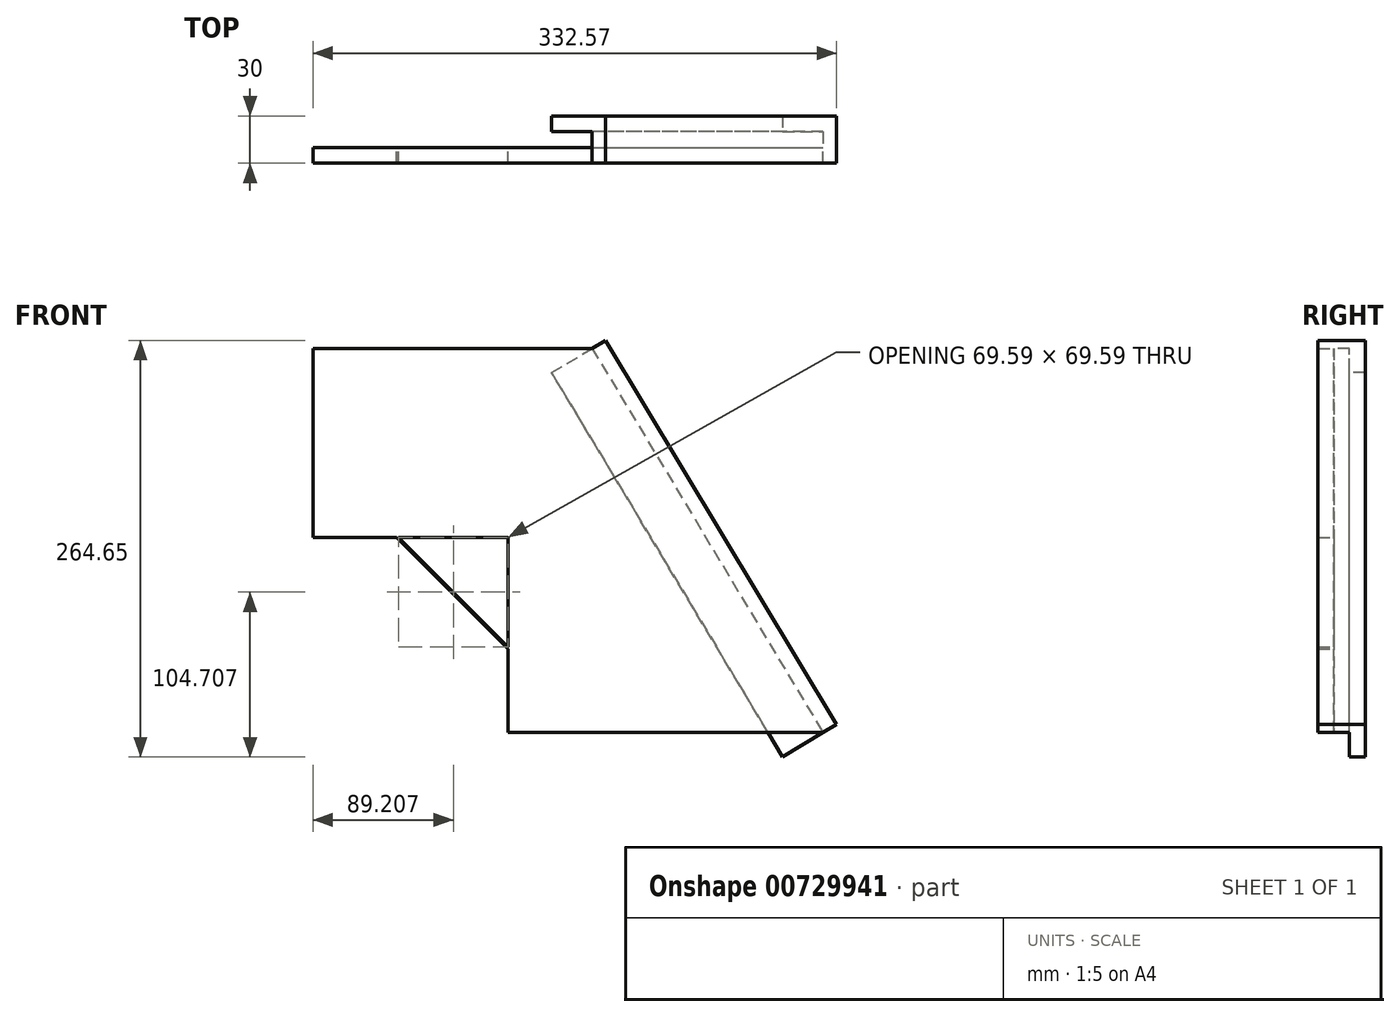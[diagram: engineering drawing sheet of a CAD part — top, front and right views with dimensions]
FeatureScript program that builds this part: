
annotation { "Feature Type Name" : "Feature", "Feature Type Description" : "" }
export const myFeature = defineFeature(function(context is Context, id is Id, definition is map)
    precondition{}
    {
        {
            var Q0;
            Q0=qCreatedBy(makeId("Front.planeOp"),FACE);
            var sketch = newSketch(context, id + "F0", { "sketchPlane" : qUnion([Q0])});
            skLineSegment(sketch, "E0", {"start": v(-68, 0) * mm, "end": v(-68, 120) * mm});
            skLineSegment(sketch, "E1", {"start": v(-68, 120) * mm, "end": v(109.36, 120) * mm});
            skLineSegment(sketch, "E2", {"start": v(109.36, 120) * mm, "end": v(256, -124.05) * mm});
            skLineSegment(sketch, "E3", {"start": v(56, -124.05) * mm, "end": v(56, 0) * mm});
            skLineSegment(sketch, "E4", {"start": v(56, 0) * mm, "end": v(-68, 0) * mm});
            skLineSegment(sketch, "E5", {"start": v(74.71, -80) * mm, "end": v(-76.05, -80) * mm, "construction": true});
            skLineSegment(sketch, "E6", {"start": v(-40, 25) * mm, "end": v(85.18, -100.18) * mm});
            skLineSegment(sketch, "E7", {"start": v(56, -124.05) * mm, "end": v(256, -124.05) * mm});
            skLineSegment(sketch, "E8", {"start": v(-40, 25) * mm, "end": v(-39.3, 25.7) * mm});
            skLineSegment(sketch, "E9", {"start": v(-39.3, 25.7) * mm, "end": v(85.89, -99.47) * mm});
            skLineSegment(sketch, "E10", {"start": v(85.89, -99.47) * mm, "end": v(85.18, -100.18) * mm});
            skSolve(sketch);
        }
        {
            var Q0;
            Q0 = qSketchRegion(id + "F0", true);
            var Q1;
            Q1=makeQuery(id+"F0.imprint","IMPRINT",FACE,{"disambiguationData":[TD([[makeQuery(id+"F0.imprint","IMPRINT",EDGE,{"derivedFrom":sQuery(id+"F0.wireOp",EDGE,"E0")}),-1.0]])]});
            extrude(context, id + "F1", {"entities" : qUnion([Q0, Q1]), "depth" : 10 * mm, "offsetDistance" : 25 * mm});
        }
        {
            var Q0;
            Q0=makeQuery(id+"F1.opExtrude","CAP_FACE",FACE,{"disambiguationData":[OSD([sQuery(id+"F0.wireOp",EDGE,"E0"),sQuery(id+"F0.wireOp",EDGE,"E1"),sQuery(id+"F0.wireOp",EDGE,"E2"),sQuery(id+"F0.wireOp",EDGE,"E3"),sQuery(id+"F0.wireOp",EDGE,"E4"),sQuery(id+"F0.wireOp",EDGE,"E6"),sQuery(id+"F0.wireOp",EDGE,"E7"),sQuery(id+"F0.wireOp",EDGE,"E9")])],"isStart":false});
            var sketch = newSketch(context, id + "F2", { "sketchPlane" : qUnion([Q0])});
            skLineSegment(sketch, "E11", {"start": v(109.36, 120) * mm, "end": v(117.93, 125.15) * mm});
            skLineSegment(sketch, "E12", {"start": v(117.93, 125.15) * mm, "end": v(264.57, -118.9) * mm});
            skLineSegment(sketch, "E13", {"start": v(264.57, -118.9) * mm, "end": v(256, -124.05) * mm});
            skLineSegment(sketch, "E14", {"start": v(256, -124.05) * mm, "end": v(109.36, 120) * mm});
            skSolve(sketch);
        }
        {
            var Q0;
            Q0=makeQuery(id+"F2.imprint","IMPRINT",FACE,{"disambiguationData":[TD([[makeQuery(id+"F2.imprint","IMPRINT",EDGE,{"derivedFrom":sQuery(id+"F2.wireOp",EDGE,"E11")}),-1.0]])]});
            extrude(context, id + "F3", {"entities" : qUnion([Q0]), "operationType" : NewBodyOperationType.ADD, "oppositeDirection" : true, "depth" : 30 * mm, "offsetDistance" : 25 * mm});
        }
        {
            var Q0;
            Q0=makeQuery(id+"F3.opExtrude","SWEPT_FACE",FACE,{"disambiguationData":[OSD([sQuery(id+"F2.wireOp",EDGE,"E14")])]});
            var sketch = newSketch(context, id + "F4", { "sketchPlane" : qUnion([Q0])});
            skLineSegment(sketch, "E15.bottom", {"start": v(-20, -238.18) * mm, "end": v(-10, -238.18) * mm});
            skLineSegment(sketch, "E15.top", {"start": v(-20, 46.54) * mm, "end": v(-10, 46.54) * mm});
            skLineSegment(sketch, "E15.left", {"start": v(-20, -238.18) * mm, "end": v(-20, 46.54) * mm});
            skLineSegment(sketch, "E15.right", {"start": v(-10, -238.18) * mm, "end": v(-10, 46.54) * mm});
            skSolve(sketch);
        }
        {
            var Q0;
            Q0=makeQuery(id+"F4.imprint","IMPRINT",FACE,{"disambiguationData":[TD([[makeQuery(id+"F4.imprint","IMPRINT",EDGE,{"derivedFrom":sQuery(id+"F4.wireOp",EDGE,"E15.bottom")}),1.0]])]});
            extrude(context, id + "F5", {"entities" : qUnion([Q0]), "operationType" : NewBodyOperationType.ADD, "depth" : 30 * mm, "offsetDistance" : 25 * mm});
        }
    });
